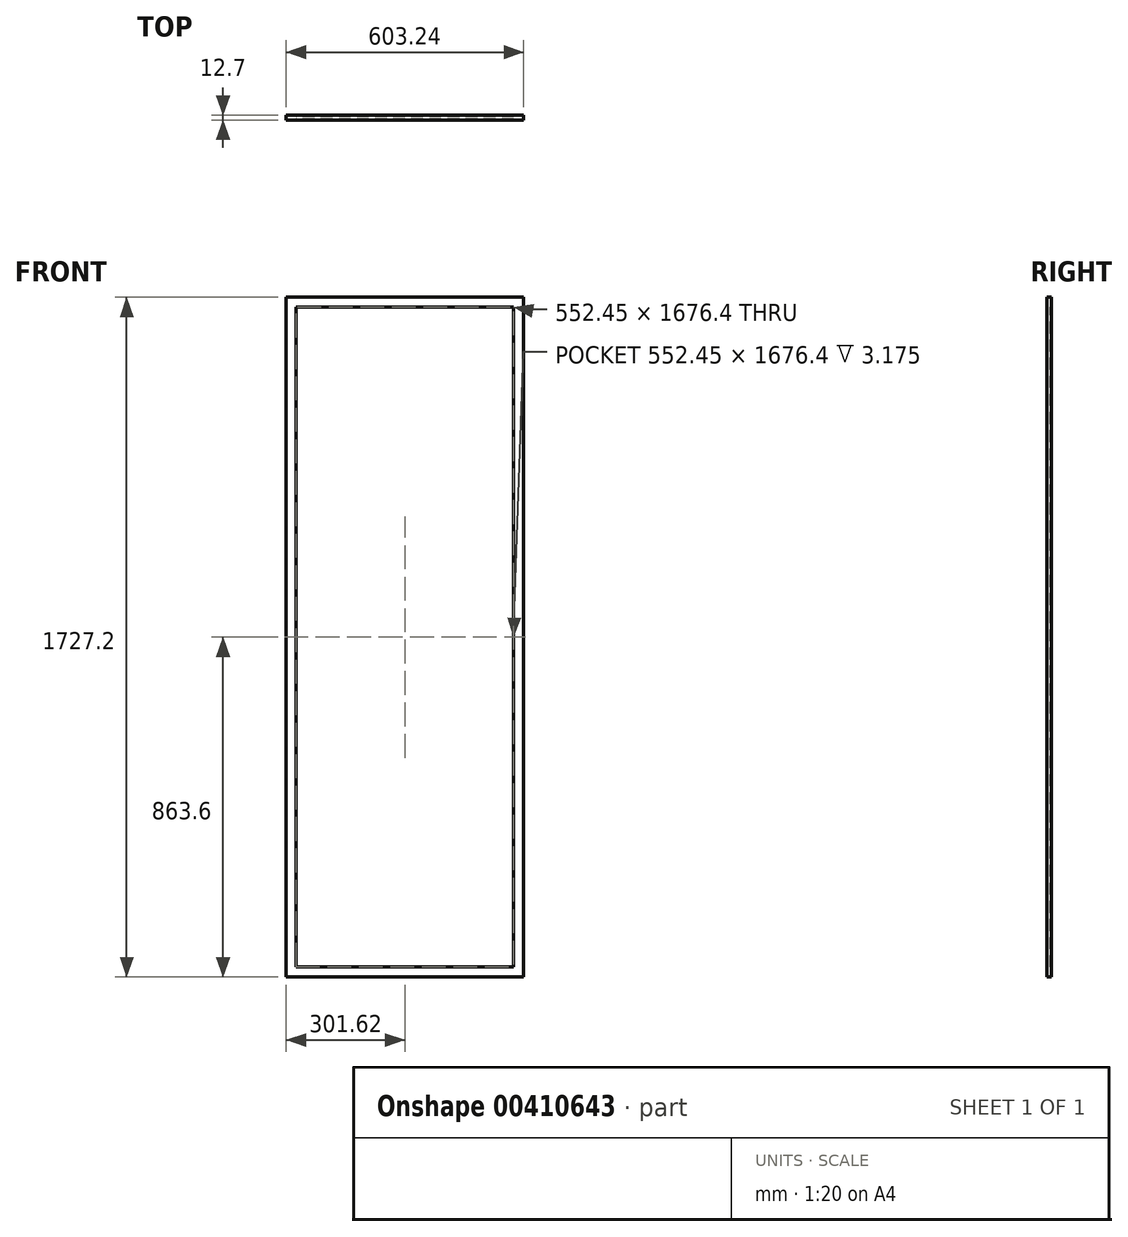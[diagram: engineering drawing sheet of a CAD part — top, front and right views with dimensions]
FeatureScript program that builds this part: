
annotation { "Feature Type Name" : "Feature", "Feature Type Description" : "" }
export const myFeature = defineFeature(function(context is Context, id is Id, definition is map)
    precondition{}
    {
        {
            var Q0;
            Q0=qCreatedBy(makeId("Front.planeOp"),FACE);
            var sketch = newSketch(context, id + "F0", { "sketchPlane" : qUnion([Q0])});
            skLineSegment(sketch, "E0.bottom", {"start": v(301.62, -863.6) * mm, "end": v(-301.63, -863.6) * mm});
            skLineSegment(sketch, "E0.top", {"start": v(301.63, 863.6) * mm, "end": v(-301.62, 863.6) * mm});
            skLineSegment(sketch, "E0.left", {"start": v(301.62, -863.6) * mm, "end": v(301.63, 863.6) * mm});
            skLineSegment(sketch, "E0.right", {"start": v(-301.63, -863.6) * mm, "end": v(-301.62, 863.6) * mm});
            skPoint(sketch, "E0.middle", {"position": v(0, 0) * mm});
            skLineSegment(sketch, "E1.0", {"start": v(-276.23, -838.2) * mm, "end": v(-276.23, 838.2) * mm});
            skLineSegment(sketch, "E1.1", {"start": v(276.22, -838.2) * mm, "end": v(-276.23, -838.2) * mm});
            skLineSegment(sketch, "E1.2", {"start": v(276.23, -838.2) * mm, "end": v(276.23, 838.2) * mm});
            skLineSegment(sketch, "E1.3", {"start": v(276.23, 838.2) * mm, "end": v(-276.23, 838.2) * mm});
            skSolve(sketch);
        }
        {
            var Q0;
            Q0 = qSketchRegion(id + "F0", true);
            extrude(context, id + "F1", {"entities" : qUnion([Q0]), "endBound" : BoundingType.SYMMETRIC, "depth" : 12.7 * mm});
        }
        {
            var Q0;
            Q0=makeQuery(id+"F0.imprint","IMPRINT",FACE,{"disambiguationData":[TD([[makeQuery(id+"F0.imprint","IMPRINT",EDGE,{"derivedFrom":sQuery(id+"F0.wireOp",EDGE,"E1.0")}),-1.0]])]});
            extrude(context, id + "F2", {"entities" : qUnion([Q0]), "operationType" : NewBodyOperationType.ADD, "endBound" : BoundingType.SYMMETRIC, "depth" : 6.35 * mm});
        }
    });
